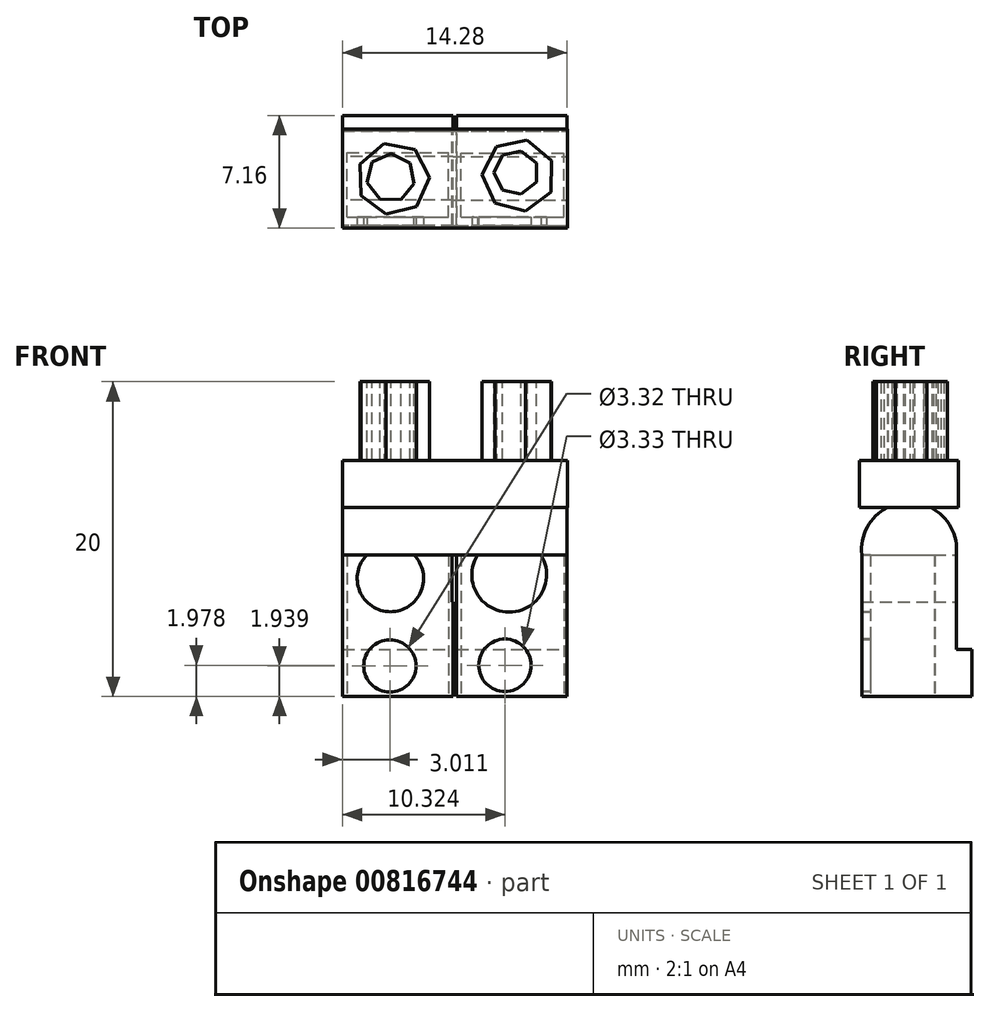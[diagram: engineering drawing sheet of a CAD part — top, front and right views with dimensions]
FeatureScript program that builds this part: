
annotation { "Feature Type Name" : "Feature", "Feature Type Description" : "" }
export const myFeature = defineFeature(function(context is Context, id is Id, definition is map)
    precondition{}
    {
        {
            var Q0;
            Q0=qCreatedBy(makeId("Top.planeOp"),FACE);
            var sketch = newSketch(context, id + "F0", { "sketchPlane" : qUnion([Q0])});
            skLineSegment(sketch, "E0.bottom", {"start": v(-0.51, 0) * mm, "end": v(-7.51, 0) * mm});
            skLineSegment(sketch, "E0.top", {"start": v(-0.51, 7) * mm, "end": v(-7.51, 7) * mm});
            skLineSegment(sketch, "E0.left", {"start": v(-0.51, 0) * mm, "end": v(-0.51, 7) * mm});
            skLineSegment(sketch, "E0.right", {"start": v(-7.51, 0) * mm, "end": v(-7.51, 7) * mm});
            skLineSegment(sketch, "E1.bottom", {"start": v(-0.27, 7) * mm, "end": v(6.73, 7) * mm});
            skLineSegment(sketch, "E1.top", {"start": v(-0.27, 0) * mm, "end": v(6.73, 0) * mm});
            skLineSegment(sketch, "E1.left", {"start": v(-0.27, 7) * mm, "end": v(-0.27, 0) * mm});
            skLineSegment(sketch, "E1.right", {"start": v(6.73, 7) * mm, "end": v(6.73, 0) * mm});
            skSolve(sketch);
        }
        {
            var Q0;
            Q0=makeQuery(id+"F0.imprint","IMPRINT",FACE,{"disambiguationData":[TD([[makeQuery(id+"F0.imprint","IMPRINT",EDGE,{"derivedFrom":sQuery(id+"F0.wireOp",EDGE,"E0.bottom")}),-1.0]])]});
            var Q1;
            Q1=makeQuery(id+"F0.imprint","IMPRINT",FACE,{"disambiguationData":[TD([[makeQuery(id+"F0.imprint","IMPRINT",EDGE,{"derivedFrom":sQuery(id+"F0.wireOp",EDGE,"E1.bottom")}),-1.0]])]});
            extrude(context, id + "F1", {"entities" : qUnion([Q0, Q1]), "depth" : 3 * mm, "offsetDistance" : 25 * mm});
        }
        {
            var Q0;
            Q0=makeQuery(id+"F1.opExtrude","CAP_FACE",FACE,{"disambiguationData":[OSD([sQuery(id+"F0.wireOp",EDGE,"E0.bottom"),sQuery(id+"F0.wireOp",EDGE,"E0.top"),sQuery(id+"F0.wireOp",EDGE,"E0.left"),sQuery(id+"F0.wireOp",EDGE,"E0.right")])],"isStart":false});
            var sketch = newSketch(context, id + "F2", { "sketchPlane" : qUnion([Q0])});
            skLineSegment(sketch, "E2", {"start": v(-7.51, 6) * mm, "end": v(-0.51, 6) * mm});
            skLineSegment(sketch, "E3", {"start": v(-0.51, 6) * mm, "end": v(-0.51, 0) * mm});
            skLineSegment(sketch, "E4", {"start": v(-0.51, 0) * mm, "end": v(-7.51, 0) * mm});
            skLineSegment(sketch, "E5", {"start": v(-7.51, 0) * mm, "end": v(-7.51, 6) * mm});
            skSolve(sketch);
        }
        {
            var Q0;
            Q0 = qSketchRegion(id + "F2", true);
            extrude(context, id + "F3", {"entities" : qUnion([Q0]), "operationType" : NewBodyOperationType.ADD, "depth" : 6 * mm, "offsetDistance" : 25 * mm});
        }
        {
            var Q0;
            Q0=makeQuery(id+"F1.opExtrude","CAP_FACE",FACE,{"disambiguationData":[OSD([sQuery(id+"F0.wireOp",EDGE,"E1.bottom"),sQuery(id+"F0.wireOp",EDGE,"E1.top"),sQuery(id+"F0.wireOp",EDGE,"E1.left"),sQuery(id+"F0.wireOp",EDGE,"E1.right")])],"isStart":false});
            var sketch = newSketch(context, id + "F4", { "sketchPlane" : qUnion([Q0])});
            skLineSegment(sketch, "E6", {"start": v(-0.27, 5.65) * mm, "end": v(6.73, 5.65) * mm});
            skLineSegment(sketch, "E7", {"start": v(6.73, 5.65) * mm, "end": v(6.73, 0) * mm});
            skLineSegment(sketch, "E8", {"start": v(6.73, 0) * mm, "end": v(-0.27, 0) * mm});
            skLineSegment(sketch, "E9", {"start": v(-0.27, 0) * mm, "end": v(-0.27, 5.65) * mm});
            skSolve(sketch);
        }
        {
            var Q0;
            Q0=makeQuery(id+"F4.imprint","IMPRINT",FACE,{"disambiguationData":[TD([[makeQuery(id+"F4.imprint","IMPRINT",EDGE,{"derivedFrom":sQuery(id+"F4.wireOp",EDGE,"E6")}),-1.0]])]});
            extrude(context, id + "F5", {"entities" : qUnion([Q0]), "operationType" : NewBodyOperationType.ADD, "depth" : 6 * mm, "offsetDistance" : 25 * mm});
        }
        {
            var Q0;
            Q0=makeQuery(id+"F3.boolean.opBoolean","MERGE",FACE,{"derivedFrom":[makeQuery(id+"F1.opExtrude","SWEPT_FACE",FACE,{"disambiguationData":[OSD([sQuery(id+"F0.wireOp",EDGE,"E0.right")])]}),makeQuery(id+"F3.opExtrude","SWEPT_FACE",FACE,{"disambiguationData":[OSD([sQuery(id+"F2.wireOp",EDGE,"E5")])]})]});
            var sketch = newSketch(context, id + "F6", { "sketchPlane" : qUnion([Q0])});
            skCircle(sketch, "E10", {"center": v(-3, 9.32) * mm, "radius": 3.02 * mm});
            skPoint(sketch, "E10.first.point", {"position": v(-6, 9) * mm});
            skPoint(sketch, "E10.second.point", {"position": v(0, 9.64) * mm});
            skPoint(sketch, "E10.third.point", {"position": v(0, 9) * mm});
            skSolve(sketch);
        }
        {
            var Q0;
            {var subQ1=sQuery(id+"F2.wireOp",EDGE,"E5");var subQ3=makeQuery(id+"F3.opExtrude","CAP_EDGE",EDGE,{"disambiguationData":[OSD([subQ1])],"isStart":false});Q0=makeQuery(id+"F6.imprint","IMPRINT",FACE,{"disambiguationData":[TD([[makeQuery(id+"F6.imprint","IMPRINT",EDGE,{"derivedFrom":subQ3}),-1.0]])]});}
            extrude(context, id + "F7", {"entities" : qUnion([Q0]), "operationType" : NewBodyOperationType.ADD, "oppositeDirection" : true, "depth" : 7 * mm, "offsetDistance" : 25 * mm});
        }
        {
            var Q0;
            Q0=makeQuery(id+"F5.boolean.opBoolean","MERGE",FACE,{"derivedFrom":[makeQuery(id+"F1.opExtrude","SWEPT_FACE",FACE,{"disambiguationData":[OSD([sQuery(id+"F0.wireOp",EDGE,"E1.right")])]}),makeQuery(id+"F5.opExtrude","SWEPT_FACE",FACE,{"disambiguationData":[OSD([sQuery(id+"F4.wireOp",EDGE,"E7")])]})]});
            var sketch = newSketch(context, id + "F8", { "sketchPlane" : qUnion([Q0])});
            skLineSegment(sketch, "E11", {"start": v(5.65, 3) * mm, "end": v(6, 3) * mm});
            skLineSegment(sketch, "E12", {"start": v(6, 3) * mm, "end": v(6, 3.5) * mm});
            skLineSegment(sketch, "E13", {"start": v(6, 3.5) * mm, "end": v(5.65, 3.5) * mm});
            skLineSegment(sketch, "E14", {"start": v(5.65, 3.5) * mm, "end": v(5.65, 3) * mm});
            skSolve(sketch);
        }
        {
            var Q0;
            Q0=makeQuery(id+"F8.imprint","IMPRINT",FACE,{"disambiguationData":[TD([[makeQuery(id+"F8.imprint","IMPRINT",EDGE,{"derivedFrom":sQuery(id+"F8.wireOp",EDGE,"E11")}),-1.0]])]});
            extrude(context, id + "F9", {"entities" : qUnion([Q0]), "operationType" : NewBodyOperationType.ADD, "oppositeDirection" : true, "depth" : 7 * mm, "offsetDistance" : 25 * mm});
        }
        {
            var Q0;
            Q0=makeQuery(id+"F9.opExtrude","SWEPT_FACE",FACE,{"disambiguationData":[OSD([sQuery(id+"F8.wireOp",EDGE,"E13")])]});
            extrude(context, id + "F10", {"entities" : qUnion([Q0]), "operationType" : NewBodyOperationType.ADD, "depth" : 5.5 * mm, "offsetDistance" : 25 * mm});
        }
        {
            var Q0;
            {var subQ0=sQuery(id+"F8.wireOp",EDGE,"E13");Q0=makeQuery(id+"F10.boolean.opBoolean","MERGE",FACE,{"derivedFrom":[makeQuery(id+"F9.boolean.opBoolean","MERGE",FACE,{"derivedFrom":[makeQuery(id+"F5.boolean.opBoolean","MERGE",FACE,{"derivedFrom":[makeQuery(id+"F1.opExtrude","SWEPT_FACE",FACE,{"disambiguationData":[OSD([sQuery(id+"F0.wireOp",EDGE,"E1.right")])]}),makeQuery(id+"F5.opExtrude","SWEPT_FACE",FACE,{"disambiguationData":[OSD([sQuery(id+"F4.wireOp",EDGE,"E7")])]})]}),makeQuery(id+"F9.opExtrude","CAP_FACE",FACE,{"disambiguationData":[OSD([sQuery(id+"F8.wireOp",EDGE,"E11"),sQuery(id+"F8.wireOp",EDGE,"E12"),subQ0,sQuery(id+"F8.wireOp",EDGE,"E14")])],"isStart":true})]}),makeQuery(id+"F10.opExtrude","SWEPT_FACE",FACE,{"disambiguationData":[OSD([subQ0]),TDD([makeQuery(id+"F9.opExtrude","CAP_EDGE",EDGE,{"disambiguationData":[OSD([subQ0])],"isStart":true})])]})]});}
            var sketch = newSketch(context, id + "F11", { "sketchPlane" : qUnion([Q0])});
            skCircle(sketch, "E15", {"center": v(3, 9.32) * mm, "radius": 3.02 * mm});
            skPoint(sketch, "E15.first.point", {"position": v(0, 9) * mm});
            skPoint(sketch, "E15.second.point", {"position": v(6, 9) * mm});
            skPoint(sketch, "E15.third.point", {"position": v(6, 9.65) * mm});
            skSolve(sketch);
        }
        {
            var Q0;
            Q0 = qSketchRegion(id + "F11", true);
            extrude(context, id + "F12", {"entities" : qUnion([Q0]), "operationType" : NewBodyOperationType.ADD, "oppositeDirection" : true, "depth" : 9 * mm, "offsetDistance" : 25 * mm});
        }
        {
            var Q0;
            Q0=makeQuery(id+"F1.opExtrude","CAP_FACE",FACE,{"disambiguationData":[OSD([sQuery(id+"F0.wireOp",EDGE,"E0.bottom"),sQuery(id+"F0.wireOp",EDGE,"E0.top"),sQuery(id+"F0.wireOp",EDGE,"E0.left"),sQuery(id+"F0.wireOp",EDGE,"E0.right")])],"isStart":true});
            cPlane(context, id + "F13", {"entities" : qUnion([Q0]), "cplaneType" : CPlaneType.OFFSET, "offset" : 15 * mm, "oppositeDirection" : true, "width" : 150 * mm, "height" : 150 * mm});
        }
        {
            var Q0;
            Q0=qCreatedBy(id+"F13.planeOp",FACE);
            var sketch = newSketch(context, id + "F14", { "sketchPlane" : qUnion([Q0])});
            skLineSegment(sketch, "E16.bottom", {"start": v(-7.53, -6.12) * mm, "end": v(6.75, -6.12) * mm});
            skLineSegment(sketch, "E16.top", {"start": v(-7.53, 0.16) * mm, "end": v(6.75, 0.16) * mm});
            skLineSegment(sketch, "E16.left", {"start": v(-7.53, -6.12) * mm, "end": v(-7.53, 0.16) * mm});
            skLineSegment(sketch, "E16.right", {"start": v(6.75, -6.12) * mm, "end": v(6.75, 0.16) * mm});
            skSolve(sketch);
        }
        {
            var Q0;
            Q0=makeQuery(id+"F14.imprint","IMPRINT",FACE,{"disambiguationData":[TD([[makeQuery(id+"F14.imprint","IMPRINT",EDGE,{"derivedFrom":sQuery(id+"F14.wireOp",EDGE,"E16.bottom")}),1.0]])]});
            extrude(context, id + "F15", {"entities" : qUnion([Q0]), "operationType" : NewBodyOperationType.ADD, "depth" : 3 * mm, "offsetDistance" : 25 * mm});
        }
        {
            var Q0;
            {var subQ0=sQuery(id+"F8.wireOp",EDGE,"E12");Q0=makeQuery(id+"F10.boolean.opBoolean","MERGE",FACE,{"derivedFrom":[makeQuery(id+"F9.opExtrude","SWEPT_FACE",FACE,{"disambiguationData":[OSD([subQ0])]}),makeQuery(id+"F10.opExtrude","SWEPT_FACE",FACE,{"disambiguationData":[OSD([subQ0,sQuery(id+"F8.wireOp",EDGE,"E13")])]})]});}
            var sketch = newSketch(context, id + "F16", { "sketchPlane" : qUnion([Q0])});
            skLineSegment(sketch, "E17", {"start": v(0.27, 9) * mm, "end": v(0.56, 9) * mm});
            skLineSegment(sketch, "E18", {"start": v(0.56, 9) * mm, "end": v(0.56, 6) * mm});
            skLineSegment(sketch, "E19", {"start": v(0.56, 6) * mm, "end": v(0.27, 6) * mm});
            skLineSegment(sketch, "E20", {"start": v(0.27, 6) * mm, "end": v(0.27, 9) * mm});
            skSolve(sketch);
        }
        {
            var Q0;
            Q0 = qSketchRegion(id + "F16", true);
            extrude(context, id + "F17", {"entities" : qUnion([Q0]), "operationType" : NewBodyOperationType.REMOVE, "oppositeDirection" : true, "depth" : 30 * mm, "offsetDistance" : 25 * mm});
        }
        {
            var Q0;
            Q0=makeQuery(id+"F15.opExtrude","CAP_FACE",FACE,{"disambiguationData":[OSD([sQuery(id+"F14.wireOp",EDGE,"E16.bottom"),sQuery(id+"F14.wireOp",EDGE,"E16.top"),sQuery(id+"F14.wireOp",EDGE,"E16.left"),sQuery(id+"F14.wireOp",EDGE,"E16.right")])],"isStart":true});
            var sketch = newSketch(context, id + "F18", { "sketchPlane" : qUnion([Q0])});
            skLineSegment(sketch, "E21", {"start": v(-7.53, 2.98) * mm, "end": v(-4.3, 2.98) * mm});
            skLineSegment(sketch, "E22", {"start": v(6.75, 2.98) * mm, "end": v(6.75, 2.98) * mm});
            skLineSegment(sketch, "E23", {"start": v(6.75, 2.98) * mm, "end": v(3.65, 3.19) * mm});
            skPoint(sketch, "E24.0.midPoint", {"position": v(-3.51, 3.59) * mm});
            skCircle(sketch, "E25.cCircle", {"center": v(3.65, 3.19) * mm, "radius": 2.08 * mm, "construction": true});
            skLineSegment(sketch, "E25.0", {"start": v(4.2, 5.42) * mm, "end": v(5.74, 4.14) * mm});
            skLineSegment(sketch, "E25.1", {"start": v(5.74, 4.14) * mm, "end": v(5.7, 2.14) * mm});
            skLineSegment(sketch, "E25.2", {"start": v(5.7, 2.14) * mm, "end": v(4.11, 0.93) * mm});
            skLineSegment(sketch, "E25.3", {"start": v(4.11, 0.93) * mm, "end": v(2.17, 1.41) * mm});
            skLineSegment(sketch, "E25.4", {"start": v(2.17, 1.41) * mm, "end": v(1.34, 3.23) * mm});
            skLineSegment(sketch, "E25.5", {"start": v(1.34, 3.23) * mm, "end": v(2.25, 5.02) * mm});
            skLineSegment(sketch, "E25.6", {"start": v(2.25, 5.02) * mm, "end": v(4.2, 5.42) * mm});
            skPoint(sketch, "E25.0.midPoint", {"position": v(4.97, 4.78) * mm});
            skCircle(sketch, "E26.cCircle", {"center": v(-4.3, 2.98) * mm, "radius": 2.08 * mm, "construction": true});
            skLineSegment(sketch, "E26.0", {"start": v(-2.92, 4.82) * mm, "end": v(-2, 3.05) * mm});
            skLineSegment(sketch, "E26.1", {"start": v(-2, 3.05) * mm, "end": v(-2.81, 1.22) * mm});
            skLineSegment(sketch, "E26.2", {"start": v(-2.81, 1.22) * mm, "end": v(-4.75, 0.72) * mm});
            skLineSegment(sketch, "E26.3", {"start": v(-4.75, 0.72) * mm, "end": v(-6.35, 1.91) * mm});
            skLineSegment(sketch, "E26.4", {"start": v(-6.35, 1.91) * mm, "end": v(-6.4, 3.91) * mm});
            skLineSegment(sketch, "E26.5", {"start": v(-6.4, 3.91) * mm, "end": v(-4.89, 5.2) * mm});
            skLineSegment(sketch, "E26.6", {"start": v(-4.89, 5.2) * mm, "end": v(-2.92, 4.82) * mm});
            skPoint(sketch, "E26.0.midPoint", {"position": v(-2.46, 3.94) * mm});
            skSolve(sketch);
        }
        {
            var Q0;
            Q0=makeQuery(id+"F18.imprint","IMPRINT",FACE,{"disambiguationData":[TD([[makeQuery(id+"F18.imprint","IMPRINT",EDGE,{"derivedFrom":sQuery(id+"F18.wireOp",EDGE,"E26.0")}),-1.0]])]});
            var Q1;
            {var subQ3=sQuery(id+"F18.wireOp",EDGE,"E25.0");Q1=makeQuery(id+"F18.imprint","IMPRINT",FACE,{"disambiguationData":[TD([[makeQuery(id+"F18.imprint","IMPRINT",EDGE,{"derivedFrom":subQ3}),-1.0]])]});}
            extrude(context, id + "F19", {"entities" : qUnion([Q0, Q1]), "operationType" : NewBodyOperationType.ADD, "depth" : 5 * mm, "offsetDistance" : 25 * mm});
        }
        {
            var Q0;
            Q0=makeQuery(id+"F19.opExtrude","CAP_FACE",FACE,{"disambiguationData":[OSD([sQuery(id+"F18.wireOp",EDGE,"E26.0"),sQuery(id+"F18.wireOp",EDGE,"E26.1"),sQuery(id+"F18.wireOp",EDGE,"E26.2"),sQuery(id+"F18.wireOp",EDGE,"E26.3"),sQuery(id+"F18.wireOp",EDGE,"E26.4"),sQuery(id+"F18.wireOp",EDGE,"E26.5"),sQuery(id+"F18.wireOp",EDGE,"E26.6")])],"isStart":false});
            var sketch = newSketch(context, id + "F20", { "sketchPlane" : qUnion([Q0])});
            skCircle(sketch, "E27.cCircle", {"center": v(-4.46, 3.05) * mm, "radius": 1.38 * mm, "construction": true});
            skLineSegment(sketch, "E27.0", {"start": v(-3.25, 3.98) * mm, "end": v(-2.97, 2.68) * mm});
            skLineSegment(sketch, "E27.1", {"start": v(-2.97, 2.68) * mm, "end": v(-3.82, 1.66) * mm});
            skLineSegment(sketch, "E27.2", {"start": v(-3.82, 1.66) * mm, "end": v(-5.14, 1.68) * mm});
            skLineSegment(sketch, "E27.3", {"start": v(-5.14, 1.68) * mm, "end": v(-5.95, 2.73) * mm});
            skLineSegment(sketch, "E27.4", {"start": v(-5.95, 2.73) * mm, "end": v(-5.64, 4.02) * mm});
            skLineSegment(sketch, "E27.5", {"start": v(-5.64, 4.02) * mm, "end": v(-4.43, 4.57) * mm});
            skLineSegment(sketch, "E27.6", {"start": v(-4.43, 4.57) * mm, "end": v(-3.25, 3.98) * mm});
            skPoint(sketch, "E27.0.midPoint", {"position": v(-3.1, 3.33) * mm});
            skSolve(sketch);
        }
        {
            var Q0;
            Q0 = qSketchRegion(id + "F20", true);
            extrude(context, id + "F21", {"entities" : qUnion([Q0]), "operationType" : NewBodyOperationType.REMOVE, "oppositeDirection" : true, "depth" : 5 * mm, "offsetDistance" : 25 * mm});
        }
        {
            var Q0;
            Q0=makeQuery(id+"F19.opExtrude","CAP_FACE",FACE,{"disambiguationData":[OSD([sQuery(id+"F18.wireOp",EDGE,"E25.0"),sQuery(id+"F18.wireOp",EDGE,"E25.1"),sQuery(id+"F18.wireOp",EDGE,"E25.2"),sQuery(id+"F18.wireOp",EDGE,"E25.3"),sQuery(id+"F18.wireOp",EDGE,"E25.4"),sQuery(id+"F18.wireOp",EDGE,"E25.5"),sQuery(id+"F18.wireOp",EDGE,"E25.6")])],"isStart":false});
            var sketch = newSketch(context, id + "F22", { "sketchPlane" : qUnion([Q0])});
            skCircle(sketch, "E28.cCircle", {"center": v(3.51, 3.37) * mm, "radius": 1.27 * mm, "construction": true});
            skLineSegment(sketch, "E28.0", {"start": v(4.78, 3.98) * mm, "end": v(4.78, 2.76) * mm});
            skLineSegment(sketch, "E28.1", {"start": v(4.78, 2.76) * mm, "end": v(3.83, 2) * mm});
            skLineSegment(sketch, "E28.2", {"start": v(3.83, 2) * mm, "end": v(2.63, 2.27) * mm});
            skLineSegment(sketch, "E28.3", {"start": v(2.63, 2.27) * mm, "end": v(2.1, 3.37) * mm});
            skLineSegment(sketch, "E28.4", {"start": v(2.1, 3.37) * mm, "end": v(2.63, 4.47) * mm});
            skLineSegment(sketch, "E28.5", {"start": v(2.63, 4.47) * mm, "end": v(3.83, 4.74) * mm});
            skLineSegment(sketch, "E28.6", {"start": v(3.83, 4.74) * mm, "end": v(4.78, 3.98) * mm});
            skPoint(sketch, "E28.0.midPoint", {"position": v(4.78, 3.37) * mm});
            skSolve(sketch);
        }
        {
            var Q0;
            Q0=makeQuery(id+"F22.imprint","IMPRINT",FACE,{"disambiguationData":[TD([[makeQuery(id+"F22.imprint","IMPRINT",EDGE,{"derivedFrom":sQuery(id+"F22.wireOp",EDGE,"E28.0")}),-1.0]])]});
            extrude(context, id + "F23", {"entities" : qUnion([Q0]), "operationType" : NewBodyOperationType.REMOVE, "oppositeDirection" : true, "depth" : 5 * mm, "offsetDistance" : 25 * mm});
        }
        {
            var Q0;
            Q0=makeQuery(id+"F1.opExtrude","CAP_FACE",FACE,{"disambiguationData":[OSD([sQuery(id+"F0.wireOp",EDGE,"E0.bottom"),sQuery(id+"F0.wireOp",EDGE,"E0.top"),sQuery(id+"F0.wireOp",EDGE,"E0.left"),sQuery(id+"F0.wireOp",EDGE,"E0.right")])],"isStart":true});
            var sketch = newSketch(context, id + "F24", { "sketchPlane" : qUnion([Q0])});
            skLineSegment(sketch, "E29.bottom", {"start": v(0, -0.55) * mm, "end": v(6.53, -0.55) * mm});
            skLineSegment(sketch, "E29.top", {"start": v(0, -4.62) * mm, "end": v(6.53, -4.62) * mm});
            skLineSegment(sketch, "E29.left", {"start": v(0, -0.55) * mm, "end": v(0, -4.62) * mm});
            skLineSegment(sketch, "E29.right", {"start": v(6.53, -0.55) * mm, "end": v(6.53, -4.62) * mm});
            skSolve(sketch);
        }
        {
            var Q0;
            Q0 = qSketchRegion(id + "F24", true);
            extrude(context, id + "F25", {"entities" : qUnion([Q0]), "operationType" : NewBodyOperationType.REMOVE, "oppositeDirection" : true, "depth" : 9 * mm, "offsetDistance" : 25 * mm});
        }
        {
            var Q0;
            Q0=makeQuery(id+"F1.opExtrude","CAP_FACE",FACE,{"disambiguationData":[OSD([sQuery(id+"F0.wireOp",EDGE,"E0.bottom"),sQuery(id+"F0.wireOp",EDGE,"E0.top"),sQuery(id+"F0.wireOp",EDGE,"E0.left"),sQuery(id+"F0.wireOp",EDGE,"E0.right")])],"isStart":true});
            var sketch = newSketch(context, id + "F26", { "sketchPlane" : qUnion([Q0])});
            skLineSegment(sketch, "E30.bottom", {"start": v(-7.24, -0.54) * mm, "end": v(-0.79, -0.54) * mm});
            skLineSegment(sketch, "E30.top", {"start": v(-7.24, -4.63) * mm, "end": v(-0.79, -4.63) * mm});
            skLineSegment(sketch, "E30.left", {"start": v(-7.24, -0.54) * mm, "end": v(-7.24, -4.63) * mm});
            skLineSegment(sketch, "E30.right", {"start": v(-0.79, -0.54) * mm, "end": v(-0.79, -4.63) * mm});
            skSolve(sketch);
        }
        {
            var Q0;
            Q0 = qSketchRegion(id + "F26", true);
            extrude(context, id + "F27", {"entities" : qUnion([Q0]), "operationType" : NewBodyOperationType.REMOVE, "oppositeDirection" : true, "depth" : 9 * mm, "offsetDistance" : 25 * mm});
        }
        {
            var Q0;
            Q0=makeQuery(id+"F3.boolean.opBoolean","MERGE",FACE,{"derivedFrom":[makeQuery(id+"F1.opExtrude","SWEPT_FACE",FACE,{"disambiguationData":[OSD([sQuery(id+"F0.wireOp",EDGE,"E0.bottom")])]}),makeQuery(id+"F3.opExtrude","SWEPT_FACE",FACE,{"disambiguationData":[OSD([sQuery(id+"F2.wireOp",EDGE,"E4")])]})]});
            var sketch = newSketch(context, id + "F28", { "sketchPlane" : qUnion([Q0])});
            skCircle(sketch, "E31", {"center": v(-4.52, 1.94) * mm, "radius": 1.66 * mm});
            skCircle(sketch, "E32", {"center": v(-4.48, 7.5) * mm, "radius": 2.1 * mm});
            skSolve(sketch);
        }
        {
            var Q0;
            {var subQ0=sQuery(id+"F28.wireOp",EDGE,"E32");var subQ1=sQuery(id+"F2.wireOp",EDGE,"E4");var subQ2=makeQuery(id+"F7.boolean.opBoolean","MERGE",EDGE,{"derivedFrom":[makeQuery(id+"F3.opExtrude","CAP_EDGE",EDGE,{"disambiguationData":[OSD([subQ1])],"isStart":false}),makeQuery(id+"F7.opExtrude","SWEPT_EDGE",EDGE,{"disambiguationData":[OSD([sQuery(id+"F0.wireOp",EDGE,"E0.bottom"),sQuery(id+"F0.wireOp",EDGE,"E0.right"),subQ1,sQuery(id+"F2.wireOp",EDGE,"E5"),sQuery(id+"F6.wireOp",EDGE,"E10")])]})]});var subQ3=makeQuery(id+"F28.imprint","INTERSECT",VERTEX,{"disambiguationData":[OD(0.0)],"derivedFrom":[subQ2,subQ0]});Q0=makeQuery(id+"F28.imprint","IMPRINT",FACE,{"disambiguationData":[TD([[makeQuery(id+"F28.imprint","IMPRINT",EDGE,{"disambiguationData":[TD([[subQ3,-1.0]])],"derivedFrom":subQ0}),1.0]])]});}
            var Q1;
            Q1=makeQuery(id+"F28.imprint","IMPRINT",FACE,{"disambiguationData":[TD([[makeQuery(id+"F28.imprint","IMPRINT",EDGE,{"derivedFrom":sQuery(id+"F28.wireOp",EDGE,"E31")}),1.0]])]});
            extrude(context, id + "F29", {"entities" : qUnion([Q0, Q1]), "operationType" : NewBodyOperationType.REMOVE, "oppositeDirection" : true, "depth" : 2 * mm, "offsetDistance" : 25 * mm});
        }
        {
            var Q0;
            Q0=makeQuery(id+"F5.boolean.opBoolean","MERGE",FACE,{"derivedFrom":[makeQuery(id+"F1.opExtrude","SWEPT_FACE",FACE,{"disambiguationData":[OSD([sQuery(id+"F0.wireOp",EDGE,"E1.top")])]}),makeQuery(id+"F5.opExtrude","SWEPT_FACE",FACE,{"disambiguationData":[OSD([sQuery(id+"F4.wireOp",EDGE,"E8")])]})]});
            var sketch = newSketch(context, id + "F30", { "sketchPlane" : qUnion([Q0])});
            skCircle(sketch, "E33", {"center": v(3.06, 7.73) * mm, "radius": 2.37 * mm});
            skCircle(sketch, "E34", {"center": v(2.8, 1.98) * mm, "radius": 1.67 * mm});
            skSolve(sketch);
        }
        {
            var Q0;
            {var subQ0=sQuery(id+"F30.wireOp",EDGE,"E33");var subQ1=makeQuery(id+"F5.opExtrude","CAP_EDGE",EDGE,{"disambiguationData":[OSD([sQuery(id+"F4.wireOp",EDGE,"E8")])],"isStart":false});var subQ2=makeQuery(id+"F30.imprint","INTERSECT",VERTEX,{"disambiguationData":[OD(0.0)],"derivedFrom":[subQ1,subQ0]});Q0=makeQuery(id+"F30.imprint","IMPRINT",FACE,{"disambiguationData":[TD([[makeQuery(id+"F30.imprint","IMPRINT",EDGE,{"disambiguationData":[TD([[subQ2,-1.0]])],"derivedFrom":subQ0}),1.0]])]});}
            var Q1;
            Q1=makeQuery(id+"F30.imprint","IMPRINT",FACE,{"disambiguationData":[TD([[makeQuery(id+"F30.imprint","IMPRINT",EDGE,{"derivedFrom":sQuery(id+"F30.wireOp",EDGE,"E34")}),1.0]])]});
            extrude(context, id + "F31", {"entities" : qUnion([Q0, Q1]), "operationType" : NewBodyOperationType.REMOVE, "oppositeDirection" : true, "depth" : 2 * mm, "offsetDistance" : 25 * mm});
        }
    });
